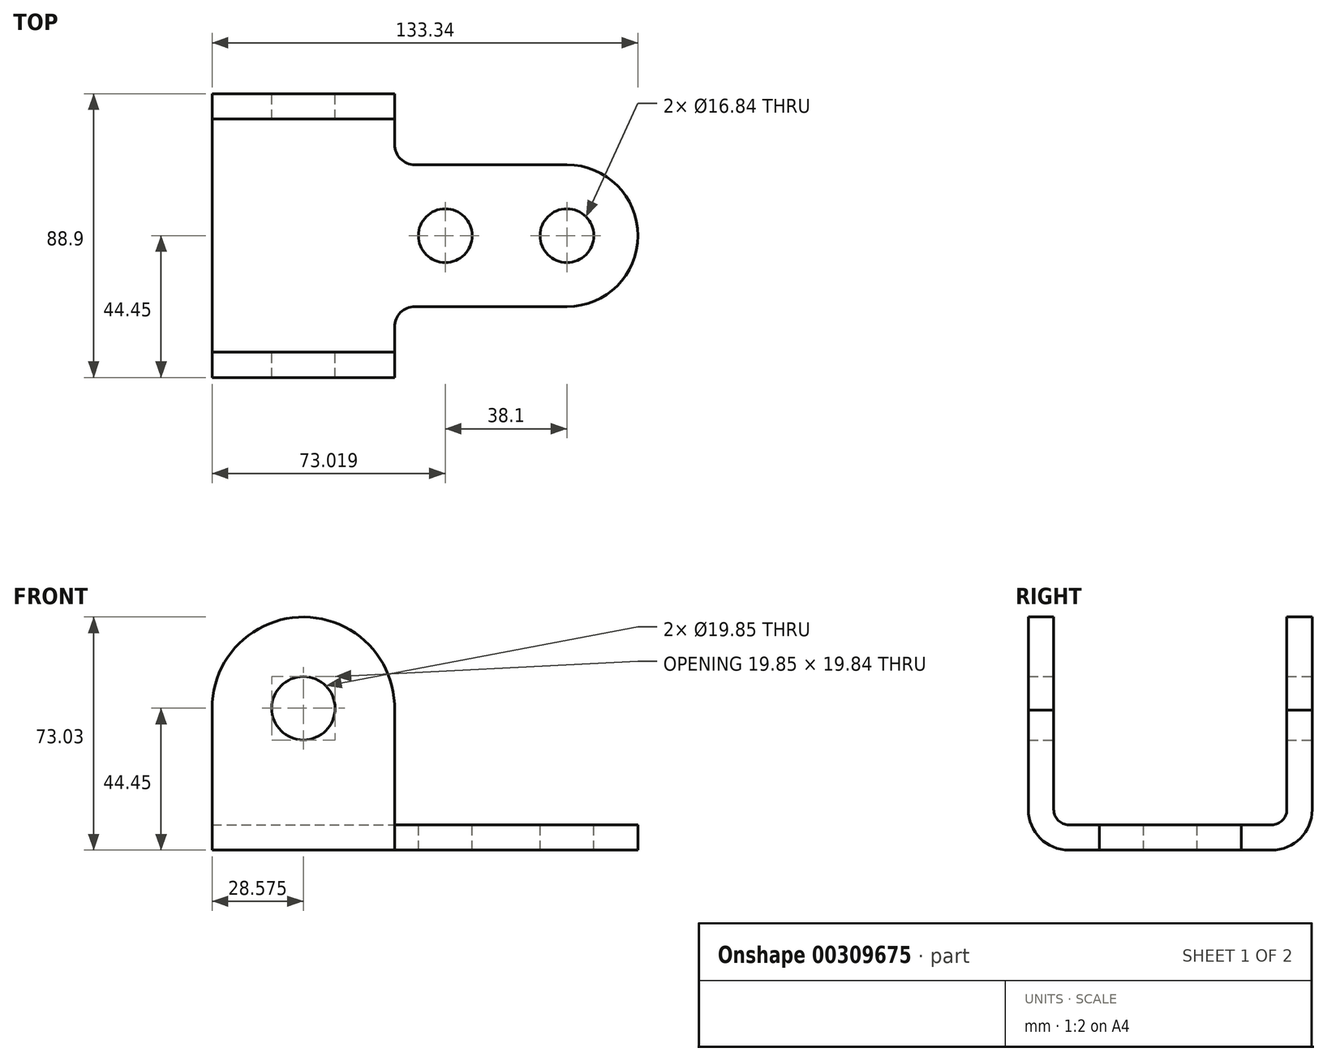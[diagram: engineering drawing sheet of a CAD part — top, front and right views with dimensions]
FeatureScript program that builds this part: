
annotation { "Feature Type Name" : "Feature", "Feature Type Description" : "" }
export const myFeature = defineFeature(function(context is Context, id is Id, definition is map)
    precondition{}
    {
        {
            var Q0;
            Q0=qCreatedBy(makeId("Front.planeOp"),FACE);
            var sketch = newSketch(context, id + "F0", { "sketchPlane" : qUnion([Q0])});
            skLineSegment(sketch, "E0", {"start": v(0, 0) * mm, "end": v(0, 44.45) * mm});
            skLineSegment(sketch, "E1", {"start": v(0, 0) * mm, "end": v(133.34, 0) * mm});
            skLineSegment(sketch, "E2", {"start": v(133.34, 0) * mm, "end": v(133.34, 7.94) * mm});
            skLineSegment(sketch, "E3", {"start": v(133.34, 7.94) * mm, "end": v(57.14, 7.94) * mm});
            skLineSegment(sketch, "E4", {"start": v(57.14, 7.94) * mm, "end": v(57.14, 43.84) * mm});
            skArc(sketch, "E5", {"start": v(0, 44.45) * mm, "mid": v(28.88, 73.02) * mm, "end": v(57.14, 43.84) * mm});
            skCircle(sketch, "E6", {"center": v(28.58, 44.45) * mm, "radius": 9.92 * mm});
            skSolve(sketch);
        }
        {
            var Q0;
            Q0 = qSketchRegion(id + "F0", true);
            extrude(context, id + "F1", {"entities" : qUnion([Q0]), "endBound" : BoundingType.SYMMETRIC, "depth" : 88.9 * mm});
        }
        {
            var Q0;
            Q0=makeQuery(id+"F1.opExtrude","SWEPT_FACE",FACE,{"disambiguationData":[OSD([sQuery(id+"F0.wireOp",EDGE,"E3")])]});
            var sketch = newSketch(context, id + "F2", { "sketchPlane" : qUnion([Q0])});
            skLineSegment(sketch, "E7", {"start": v(63.5, 22.22) * mm, "end": v(111.12, 22.22) * mm});
            skLineSegment(sketch, "E8", {"start": v(111.12, -22.23) * mm, "end": v(63.5, -22.23) * mm});
            skArc(sketch, "E9", {"start": v(111.12, 22.23) * mm, "mid": v(133.34, 0) * mm, "end": v(111.12, -22.23) * mm});
            skCircle(sketch, "E10", {"center": v(73.02, 0) * mm, "radius": 8.42 * mm});
            skCircle(sketch, "E11", {"center": v(111.12, 0) * mm, "radius": 8.42 * mm});
            skLineSegment(sketch, "E12", {"start": v(57.14, 44.45) * mm, "end": v(57.14, 28.57) * mm});
            skArc(sketch, "E13", {"start": v(57.14, 28.57) * mm, "mid": v(59, 24.08) * mm, "end": v(63.5, 22.22) * mm});
            skLineSegment(sketch, "E14", {"start": v(57.14, -44.45) * mm, "end": v(57.14, -28.58) * mm});
            skArc(sketch, "E15", {"start": v(63.5, -22.22) * mm, "mid": v(59, -24.08) * mm, "end": v(57.14, -28.58) * mm});
            skLineSegment(sketch, "E16.bottom", {"start": v(0, 36.51) * mm, "end": v(57.14, 36.51) * mm});
            skLineSegment(sketch, "E16.top", {"start": v(0, -36.51) * mm, "end": v(57.14, -36.51) * mm});
            skLineSegment(sketch, "E16.left", {"start": v(0, 36.51) * mm, "end": v(0, -36.51) * mm});
            skLineSegment(sketch, "E16.right", {"start": v(57.14, 36.51) * mm, "end": v(57.14, -36.51) * mm});
            skSolve(sketch);
        }
        {
            var Q0;
            {var subQ7=sQuery(id+"F2.wireOp",EDGE,"E7");Q0=makeQuery(id+"F2.imprint","IMPRINT",FACE,{"disambiguationData":[TD([[makeQuery(id+"F2.imprint","IMPRINT",EDGE,{"derivedFrom":subQ7}),1.0]])]});}
            var Q1;
            {var subQ7=sQuery(id+"F2.wireOp",EDGE,"E8");Q1=makeQuery(id+"F2.imprint","IMPRINT",FACE,{"disambiguationData":[TD([[makeQuery(id+"F2.imprint","IMPRINT",EDGE,{"derivedFrom":subQ7}),1.0]])]});}
            var Q2;
            Q2=makeQuery(id+"F2.imprint","IMPRINT",FACE,{"disambiguationData":[TD([[makeQuery(id+"F2.imprint","IMPRINT",EDGE,{"derivedFrom":sQuery(id+"F2.wireOp",EDGE,"E10")}),1.0]])]});
            var Q3;
            Q3=makeQuery(id+"F2.imprint","IMPRINT",FACE,{"disambiguationData":[TD([[makeQuery(id+"F2.imprint","IMPRINT",EDGE,{"derivedFrom":sQuery(id+"F2.wireOp",EDGE,"E11")}),1.0]])]});
            extrude(context, id + "F3", {"entities" : qUnion([Q0, Q1, Q2, Q3]), "operationType" : NewBodyOperationType.REMOVE, "endBound" : BoundingType.THROUGH_ALL, "oppositeDirection" : true, "depth" : 25.4 * mm});
        }
        {
            var Q0;
            {var subQ0=sQuery(id+"F2.wireOp",EDGE,"E16.right");Q0=makeQuery(id+"F3.boolean.opBoolean","MERGE",FACE,{"derivedFrom":[makeQuery(id+"F1.opExtrude","SWEPT_FACE",FACE,{"disambiguationData":[OSD([sQuery(id+"F0.wireOp",EDGE,"E4")])]}),makeQuery(id+"F3.opExtrude","SWEPT_FACE",FACE,{"disambiguationData":[OSD([sQuery(id+"F2.wireOp",EDGE,"E12"),subQ0])]}),makeQuery(id+"F3.opExtrude","SWEPT_FACE",FACE,{"disambiguationData":[OSD([sQuery(id+"F2.wireOp",EDGE,"E14"),subQ0])]})]});}
            var sketch = newSketch(context, id + "F4", { "sketchPlane" : qUnion([Q0])});
            skLineSegment(sketch, "E17.bottom", {"start": v(-36.51, 7.94) * mm, "end": v(36.51, 7.94) * mm});
            skLineSegment(sketch, "E17.top", {"start": v(-36.51, 76.54) * mm, "end": v(36.51, 76.54) * mm});
            skLineSegment(sketch, "E17.left", {"start": v(-36.51, 7.94) * mm, "end": v(-36.51, 76.54) * mm});
            skLineSegment(sketch, "E17.right", {"start": v(36.51, 7.94) * mm, "end": v(36.51, 76.54) * mm});
            skSolve(sketch);
        }
        {
            var Q0;
            Q0 = qSketchRegion(id + "F4", true);
            extrude(context, id + "F5", {"entities" : qUnion([Q0]), "operationType" : NewBodyOperationType.REMOVE, "endBound" : BoundingType.THROUGH_ALL, "oppositeDirection" : true, "depth" : 25.4 * mm, "hasSecondDirection" : true, "secondDirectionBound" : SecondDirectionBoundingType.THROUGH_ALL, "secondDirectionOppositeDirection" : false, "secondDirectionDepth" : 25.4 * mm});
        }
        {
            var Q0;
            Q0=makeQuery(id+"F1.opExtrude","CAP_EDGE",EDGE,{"disambiguationData":[OSD([sQuery(id+"F0.wireOp",EDGE,"E1")])],"isStart":false});
            var Q1;
            Q1=makeQuery(id+"F1.opExtrude","CAP_EDGE",EDGE,{"disambiguationData":[OSD([sQuery(id+"F0.wireOp",EDGE,"E1")])],"isStart":true});
            fillet(context, id + "F6", {"entities" : qUnion([Q0, Q1]), "radius" : 12.7 * mm, "tangentPropagation" : true, "allowEdgeOverflow" : false});
        }
        {
            var Q0;
            Q0=makeQuery(id+"F5.boolean.opBoolean","COPY",EDGE,{"derivedFrom":makeQuery(id+"F5.opExtrude","SWEPT_EDGE",EDGE,{"disambiguationData":[OSD([sQuery(id+"F4.wireOp",EDGE,"E17.bottom"),sQuery(id+"F4.wireOp",EDGE,"E17.right")])]})});
            var Q1;
            Q1=makeQuery(id+"F5.boolean.opBoolean","COPY",EDGE,{"derivedFrom":makeQuery(id+"F5.opExtrude","SWEPT_EDGE",EDGE,{"disambiguationData":[OSD([sQuery(id+"F4.wireOp",EDGE,"E17.bottom"),sQuery(id+"F4.wireOp",EDGE,"E17.left")])]})});
            fillet(context, id + "F7", {"entities" : qUnion([Q0, Q1]), "radius" : 4.76 * mm, "tangentPropagation" : true, "allowEdgeOverflow" : false});
        }
    });
